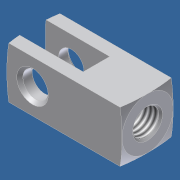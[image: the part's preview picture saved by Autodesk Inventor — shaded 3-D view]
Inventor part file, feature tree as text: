
AUTODESK INVENTOR PART (.ipt)
format: ipt  version: unknown  size: 262,656 bytes
history: native  units: in
note: dims shown in document units (in); Inventor stores cm internally (conversion verified against a paired STEP export)
features: other x126, sketch x7, revolve x5, extrude x2, thread x1
ambient origin geometry x8: Origin, YZ Plane, XZ Plane, XY Plane, X Axis, Y Axis, Z Axis, Center Point
feature tree (141):
  extrude  "Extrusion1"  Depth=0.75in TaperAngle=0.0deg
  extrude  "Extrusion2"  Depth=0.62in TaperAngle=0.0deg
  revolve  "Revolution1"  Angle=360.0deg
  thread  "Thread1"  [1 undecoded]
  revolve  "Revolution2"  [1 undecoded]
  revolve  "Revolution3"  [1 undecoded]
  revolve  "Revolution4"  [1 undecoded]
  revolve  "Revolution5"  [1 undecoded]
  other  "dummy_XY"
  other  "dummy_YZ"
  other  "dummy_ZX"
  other  "dummy_X"
  other  "dummy_Y"
  other  "dummy_Z"
  other  "dummy_Center"
  other  "h1_XY"
  other  "h1_YZ"
  other  "h1_ZX"
  other  "h1_X"
  other  "h1_Y"
  other  "h1_Z"
  other  "h1_Center"
  other  "h2_XY"
  other  "h2_YZ"
  other  "h2_ZX"
  other  "h2_X"
  other  "h2_Y"
  other  "h2_Z"
  other  "h2_Center"
  other  "l1_XY"
  other  "l1_YZ"
  other  "l1_ZX"
  other  "l1_X"
  other  "l1_Y"
  other  "l1_Z"
  other  "l1_Center"
  other  "l11_XY"
  other  "l11_YZ"
  other  "l11_ZX"
  other  "l11_X"
  other  "l11_Y"
  other  "l11_Z"
  other  "l11_Center"
  other  "l12_XY"
  other  "l12_YZ"
  other  "l12_ZX"
  other  "l12_X"
  other  "l12_Y"
  other  "l12_Z"
  other  "l12_Center"
  other  "l2_XY"
  other  "l2_YZ"
  other  "l2_ZX"
  other  "l2_X"
  other  "l2_Y"
  other  "l2_Z"
  other  "l2_Center"
  other  "l21_XY"
  other  "l21_YZ"
  other  "l21_ZX"
  other  "l21_X"
  other  "l21_Y"
  other  "l21_Z"
  other  "l21_Center"
  other  "l22_XY"
  other  "l22_YZ"
  other  "l22_ZX"
  other  "l22_X"
  other  "l22_Y"
  other  "l22_Z"
  other  "l22_Center"
  other  "piston_rod_clevis_XY"
  other  "piston_rod_clevis_YZ"
  other  "piston_rod_clevis_ZX"
  other  "piston_rod_clevis_X"
  other  "piston_rod_clevis_Y"
  other  "piston_rod_clevis_Z"
  other  "piston_rod_clevis_Center"
  other  "rod_clevis_body_XY"
  other  "rod_clevis_body_YZ"
  other  "rod_clevis_body_ZX"
  other  "rod_clevis_body_X"
  other  "rod_clevis_body_Y"
  other  "rod_clevis_body_Z"
  other  "rod_clevis_body_Center"
  other  "th1_XY"
  other  "th1_YZ"
  other  "th1_ZX"
  other  "th1_X"
  other  "th1_Y"
  other  "th1_Z"
  other  "th1_Center"
  other  "th2_XY"
  other  "th2_YZ"
  other  "th2_ZX"
  other  "th2_X"
  other  "th2_Y"
  other  "th2_Z"
  other  "th2_Center"
  other  "to_cylinder_XY"
  other  "to_cylinder_YZ"
  other  "to_cylinder_ZX"
  other  "to_cylinder_X"
  other  "to_cylinder_Y"
  other  "to_cylinder_Z"
  other  "to_cylinder_Center"
  other  "w1_XY"
  other  "w1_YZ"
  other  "w1_ZX"
  other  "w1_X"
  other  "w1_Y"
  other  "w1_Z"
  other  "w1_Center"
  other  "w11_XY"
  other  "w11_YZ"
  other  "w11_ZX"
  other  "w11_X"
  other  "w11_Y"
  other  "w11_Z"
  other  "w11_Center"
  other  "w12_XY"
  other  "w12_YZ"
  other  "w12_ZX"
  other  "w12_X"
  other  "w12_Y"
  other  "w12_Z"
  other  "w12_Center"
  other  "w2_XY"
  other  "w2_YZ"
  other  "w2_ZX"
  other  "w2_X"
  other  "w2_Y"
  other  "w2_Z"
  other  "w2_Center"
  sketch  "Sketch_1"  dims[d0=0.75in d1=0.0in d2=0.75in d3=0.0in]
  sketch  "Sketch_2"  dims[d4=360.0deg d5=0.62in d6=0.0in]
  sketch  "Sketch_3"  dims[d7=360.0deg d8=360.0deg d9=360.0deg]
  sketch  "Sketch_4"  dims[d10=360.0deg]
  sketch  "Sketch_5"
  sketch  "Sketch_9"
  sketch  "Sketch_10"
note: 5 required parameter values undecoded (feature->parameter linkage not recoverable at this tier; creation-order binding heuristic only, values carry confidence <= 0.55)
